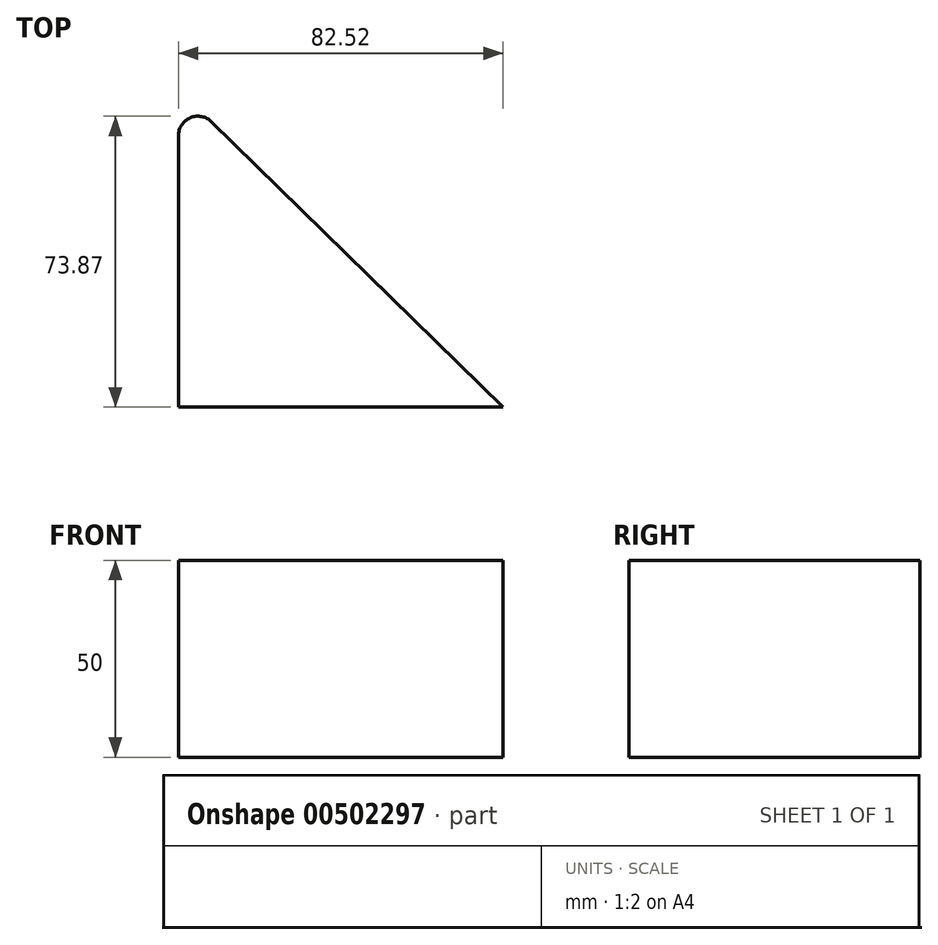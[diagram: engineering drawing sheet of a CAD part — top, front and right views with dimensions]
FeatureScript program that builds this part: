
annotation { "Feature Type Name" : "Feature", "Feature Type Description" : "" }
export const myFeature = defineFeature(function(context is Context, id is Id, definition is map)
    precondition{}
    {
        {
            var Q0;
            Q0=qCreatedBy(makeId("Top.planeOp"),FACE);
            var sketch = newSketch(context, id + "F0", { "sketchPlane" : qUnion([Q0])});
            skLineSegment(sketch, "E0", {"start": v(-39.82, 50.68) * mm, "end": v(-39.82, -30.08) * mm});
            skLineSegment(sketch, "E1", {"start": v(-39.82, -30.08) * mm, "end": v(42.7, -30.08) * mm});
            skLineSegment(sketch, "E2", {"start": v(42.7, -30.08) * mm, "end": v(-39.82, 50.68) * mm});
            skSolve(sketch);
        }
        {
            var Q0;
            Q0 = qSketchRegion(id + "F0", true);
            extrude(context, id + "F1", {"entities" : qUnion([Q0]), "endBound" : BoundingType.SYMMETRIC, "oppositeDirection" : true, "depth" : 50 * mm});
        }
        {
            var Q0;
            Q0=makeQuery(id+"F1.opExtrude","SWEPT_EDGE",EDGE,{"disambiguationData":[OSD([sQuery(id+"F0.wireOp",EDGE,"E0"),sQuery(id+"F0.wireOp",EDGE,"E2")])]});
            fillet(context, id + "F2", {"entities" : qUnion([Q0]), "radius" : 5 * mm, "tangentPropagation" : true, "allowEdgeOverflow" : false});
        }
    });
